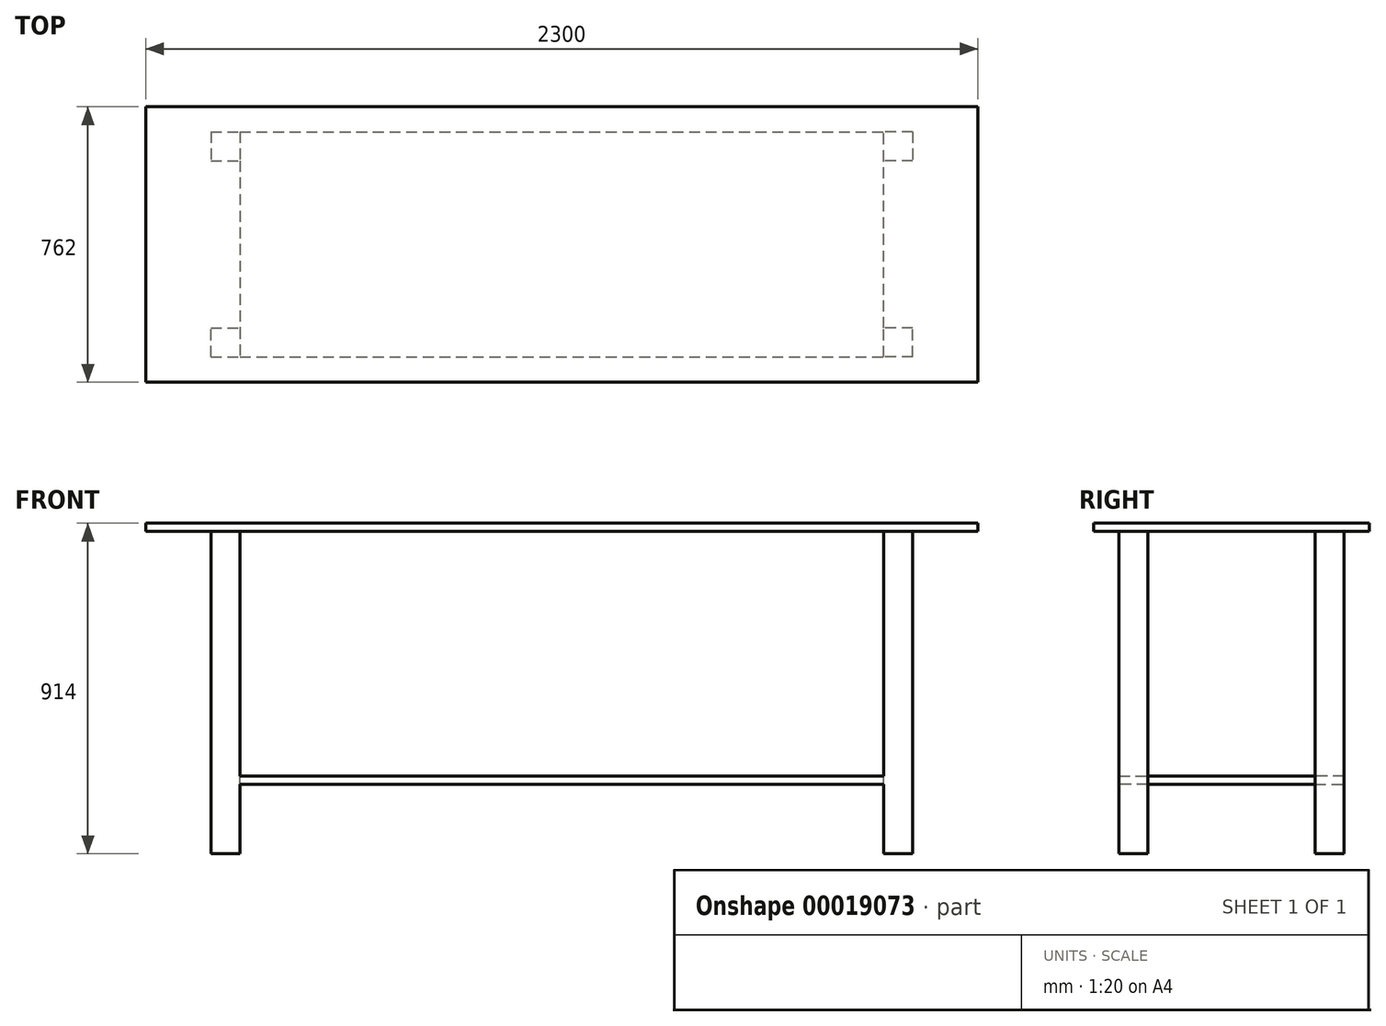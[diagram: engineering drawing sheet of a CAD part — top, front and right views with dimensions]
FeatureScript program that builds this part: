
annotation { "Feature Type Name" : "Feature", "Feature Type Description" : "" }
export const myFeature = defineFeature(function(context is Context, id is Id, definition is map)
    precondition{}
    {
        {
            var Q0;
            Q0=qCreatedBy(makeId("Top.planeOp"),FACE);
            var sketch = newSketch(context, id + "F0", { "sketchPlane" : qUnion([Q0])});
            skLineSegment(sketch, "E0.bottom", {"start": v(0, 0) * mm, "end": v(2300, 0) * mm});
            skLineSegment(sketch, "E0.top", {"start": v(0, 762) * mm, "end": v(2300, 762) * mm});
            skLineSegment(sketch, "E0.left", {"start": v(0, 0) * mm, "end": v(0, 762) * mm});
            skLineSegment(sketch, "E0.right", {"start": v(2300, 0) * mm, "end": v(2300, 762) * mm});
            skLineSegment(sketch, "E1", {"start": v(0, 381) * mm, "end": v(2300, 381) * mm, "construction": true});
            skLineSegment(sketch, "E2", {"start": v(1150, 762) * mm, "end": v(1150, 0) * mm, "construction": true});
            skLineSegment(sketch, "E3.bottom", {"start": v(180, 692) * mm, "end": v(260, 692) * mm});
            skLineSegment(sketch, "E3.top", {"start": v(180, 612) * mm, "end": v(260, 612) * mm});
            skLineSegment(sketch, "E3.left", {"start": v(180, 692) * mm, "end": v(180, 612) * mm});
            skLineSegment(sketch, "E3.right", {"start": v(260, 692) * mm, "end": v(260, 612) * mm});
            skLineSegment(sketch, "E4.MirrorCS", {"start": v(2120, 692) * mm, "end": v(2040, 692) * mm});
            skLineSegment(sketch, "E5.MirrorCS", {"start": v(2120, 612) * mm, "end": v(2040, 612) * mm});
            skLineSegment(sketch, "E6.MirrorCS", {"start": v(2120, 692) * mm, "end": v(2120, 612) * mm});
            skLineSegment(sketch, "E7.MirrorCS", {"start": v(2040, 692) * mm, "end": v(2040, 612) * mm});
            skLineSegment(sketch, "E8.MirrorCS", {"start": v(2040, 70) * mm, "end": v(2040, 150) * mm});
            skLineSegment(sketch, "E9.MirrorCS", {"start": v(2120, 70) * mm, "end": v(2120, 150) * mm});
            skLineSegment(sketch, "E10.MirrorCS", {"start": v(2120, 150) * mm, "end": v(2040, 150) * mm});
            skLineSegment(sketch, "E11.MirrorCS", {"start": v(2120, 70) * mm, "end": v(2040, 70) * mm});
            skLineSegment(sketch, "E12.MirrorCS", {"start": v(260, 70) * mm, "end": v(260, 150) * mm});
            skLineSegment(sketch, "E13.MirrorCS", {"start": v(180, 70) * mm, "end": v(180, 150) * mm});
            skLineSegment(sketch, "E14.MirrorCS", {"start": v(180, 150) * mm, "end": v(260, 150) * mm});
            skLineSegment(sketch, "E15.MirrorCS", {"start": v(180, 70) * mm, "end": v(260, 70) * mm});
            skLineSegment(sketch, "E16.bottom", {"start": v(260, 692) * mm, "end": v(2040, 692) * mm});
            skLineSegment(sketch, "E16.top", {"start": v(260, 70) * mm, "end": v(2040, 70) * mm});
            skLineSegment(sketch, "E16.left", {"start": v(260, 692) * mm, "end": v(260, 70) * mm});
            skLineSegment(sketch, "E16.right", {"start": v(2040, 692) * mm, "end": v(2040, 70) * mm});
            skSolve(sketch);
        }
        {
            var Q0;
            {var subQ4=sQuery(id+"F0.wireOp",EDGE,"E16.bottom");Q0=makeQuery(id+"F0.imprint","IMPRINT",FACE,{"disambiguationData":[TD([[makeQuery(id+"F0.imprint","IMPRINT",EDGE,{"derivedFrom":subQ4}),-1.0]])]});}
            var Q1;
            {var subQ2=sQuery(id+"F0.wireOp",EDGE,"E3.bottom");Q1=makeQuery(id+"F0.imprint","IMPRINT",FACE,{"disambiguationData":[TD([[makeQuery(id+"F0.imprint","IMPRINT",EDGE,{"derivedFrom":subQ2}),-1.0]])]});}
            var Q2;
            Q2=makeQuery(id+"F0.imprint","IMPRINT",FACE,{"disambiguationData":[TD([[makeQuery(id+"F0.imprint","IMPRINT",EDGE,{"derivedFrom":sQuery(id+"F0.wireOp",EDGE,"E13.MirrorCS")}),-1.0]])]});
            var Q3;
            Q3=makeQuery(id+"F0.imprint","IMPRINT",FACE,{"disambiguationData":[TD([[makeQuery(id+"F0.imprint","IMPRINT",EDGE,{"derivedFrom":sQuery(id+"F0.wireOp",EDGE,"E0.bottom")}),1.0]])]});
            var Q4;
            Q4=makeQuery(id+"F0.imprint","IMPRINT",FACE,{"disambiguationData":[TD([[makeQuery(id+"F0.imprint","IMPRINT",EDGE,{"derivedFrom":sQuery(id+"F0.wireOp",EDGE,"E9.MirrorCS")}),1.0]])]});
            var Q5;
            {var subQ2=sQuery(id+"F0.wireOp",EDGE,"E4.MirrorCS");Q5=makeQuery(id+"F0.imprint","IMPRINT",FACE,{"disambiguationData":[TD([[makeQuery(id+"F0.imprint","IMPRINT",EDGE,{"derivedFrom":subQ2}),1.0]])]});}
            extrude(context, id + "F1", {"entities" : qUnion([Q0, Q1, Q2, Q3, Q4, Q5]), "depth" : 22 * mm});
        }
        {
            var Q0;
            Q0=makeQuery(id+"F0.imprint","IMPRINT",FACE,{"disambiguationData":[TD([[makeQuery(id+"F0.imprint","IMPRINT",EDGE,{"derivedFrom":sQuery(id+"F0.wireOp",EDGE,"E13.MirrorCS")}),-1.0]])]});
            var Q1;
            {var subQ2=sQuery(id+"F0.wireOp",EDGE,"E3.bottom");Q1=makeQuery(id+"F0.imprint","IMPRINT",FACE,{"disambiguationData":[TD([[makeQuery(id+"F0.imprint","IMPRINT",EDGE,{"derivedFrom":subQ2}),-1.0]])]});}
            var Q2;
            Q2=makeQuery(id+"F0.imprint","IMPRINT",FACE,{"disambiguationData":[TD([[makeQuery(id+"F0.imprint","IMPRINT",EDGE,{"derivedFrom":sQuery(id+"F0.wireOp",EDGE,"E9.MirrorCS")}),1.0]])]});
            var Q3;
            {var subQ2=sQuery(id+"F0.wireOp",EDGE,"E4.MirrorCS");Q3=makeQuery(id+"F0.imprint","IMPRINT",FACE,{"disambiguationData":[TD([[makeQuery(id+"F0.imprint","IMPRINT",EDGE,{"derivedFrom":subQ2}),1.0]])]});}
            extrude(context, id + "F2", {"entities" : qUnion([Q0, Q1, Q2, Q3]), "operationType" : NewBodyOperationType.ADD, "oppositeDirection" : true, "depth" : (914 - 22) * mm});
        }
        {
            var Q0;
            {var subQ4=sQuery(id+"F0.wireOp",EDGE,"E16.bottom");Q0=makeQuery(id+"F0.imprint","IMPRINT",FACE,{"disambiguationData":[TD([[makeQuery(id+"F0.imprint","IMPRINT",EDGE,{"derivedFrom":subQ4}),-1.0]])]});}
            extrude(context, id + "F3", {"entities" : qUnion([Q0]), "operationType" : NewBodyOperationType.ADD, "oppositeDirection" : true, "depth" : 700 * mm, "hasSecondDirection" : true, "secondDirectionOppositeDirection" : true, "secondDirectionDepth" : (700 - 22) * mm});
        }
    });
